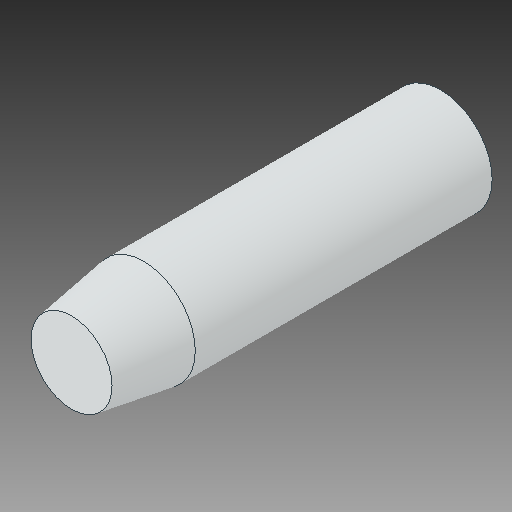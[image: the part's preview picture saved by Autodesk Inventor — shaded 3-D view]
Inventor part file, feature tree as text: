
AUTODESK INVENTOR PART (.ipt)
format: ipt  version: 2018 (Build 220112000, 112)  size: 96,256 bytes
history: native  units: in
note: dims shown in document units (in); Inventor stores cm internally (conversion verified against a paired STEP export)
features: chamfer x1
ambient origin geometry x8: Origin, YZ Plane, XZ Plane, XY Plane, X Axis, Y Axis, Z Axis, Center Point
bodies: Solid1 (feature_tree)
feature tree (1):
  chamfer  "Chamfer1"  [1 undecoded]
note: 1 required parameter value undecoded (feature->parameter linkage not recoverable at this tier; creation-order binding heuristic only, values carry confidence <= 0.55)
